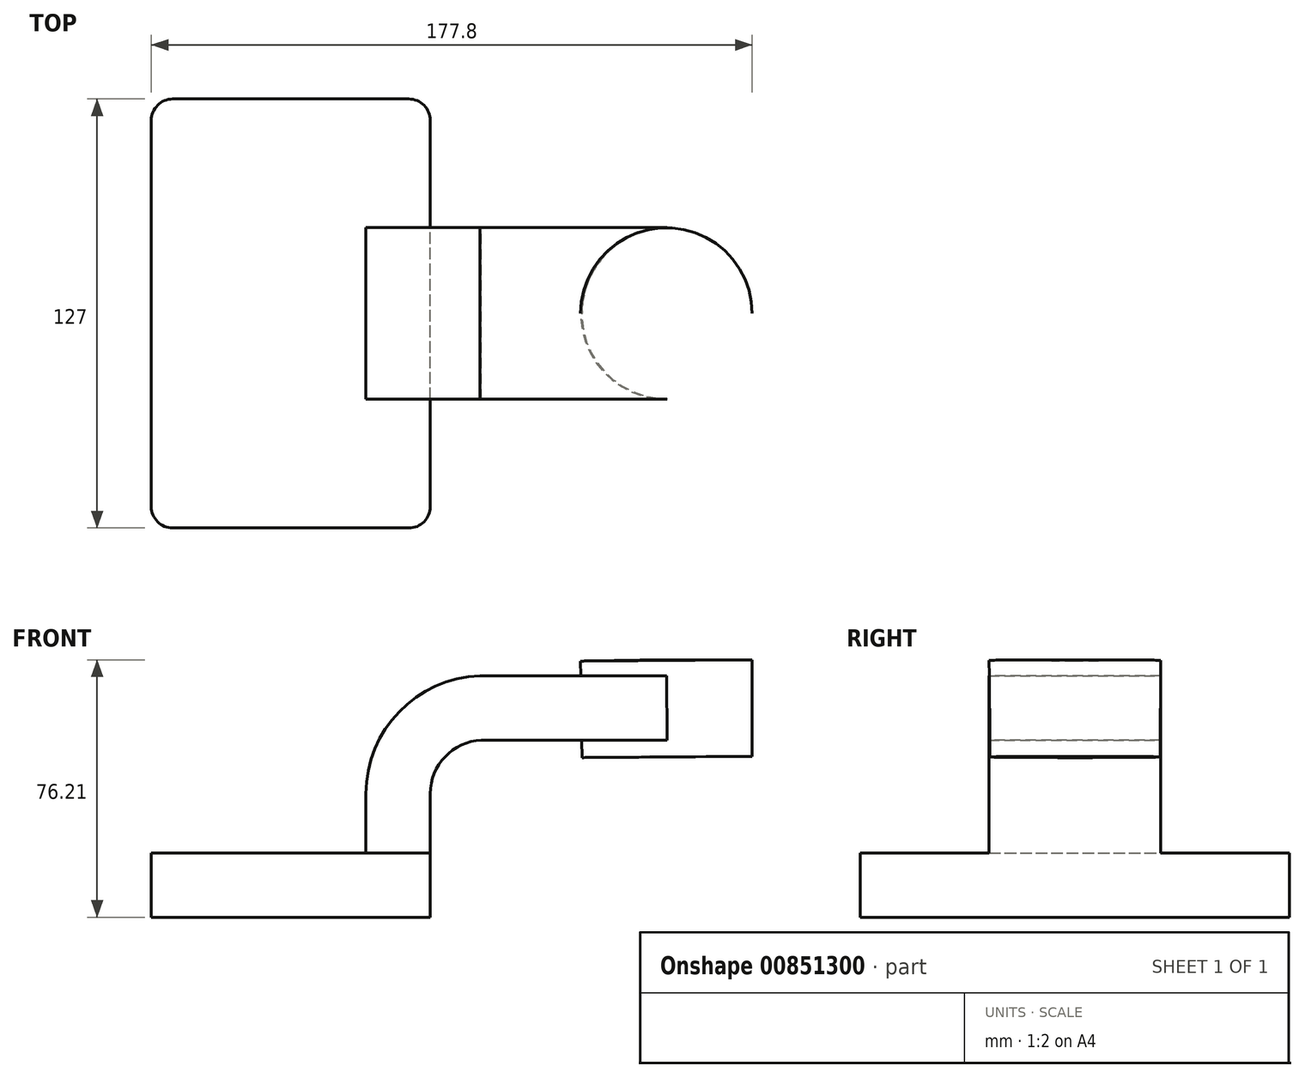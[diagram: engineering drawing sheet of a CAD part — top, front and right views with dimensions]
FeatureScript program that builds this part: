
annotation { "Feature Type Name" : "Feature", "Feature Type Description" : "" }
export const myFeature = defineFeature(function(context is Context, id is Id, definition is map)
    precondition{}
    {
        {
            var Q0;
            Q0=qCreatedBy(makeId("Front.planeOp"),FACE);
            var sketch = newSketch(context, id + "F0", { "sketchPlane" : qUnion([Q0])});
            skLineSegment(sketch, "E0.bottom", {"start": v(-41.28, -9.53) * mm, "end": v(41.28, -9.53) * mm});
            skLineSegment(sketch, "E0.top", {"start": v(-41.28, 9.53) * mm, "end": v(41.28, 9.53) * mm});
            skLineSegment(sketch, "E0.left", {"start": v(-41.28, -9.53) * mm, "end": v(-41.28, 9.53) * mm});
            skLineSegment(sketch, "E0.right", {"start": v(41.28, -9.53) * mm, "end": v(41.28, 9.52) * mm});
            skPoint(sketch, "E0.middle", {"position": v(0, 0) * mm});
            skLineSegment(sketch, "E1.bottom", {"start": v(85.72, 66.67) * mm, "end": v(136.53, 66.67) * mm});
            skLineSegment(sketch, "E1.top", {"start": v(85.72, 38.1) * mm, "end": v(136.53, 38.1) * mm});
            skLineSegment(sketch, "E1.left", {"start": v(85.72, 66.68) * mm, "end": v(85.72, 38.1) * mm});
            skLineSegment(sketch, "E1.right", {"start": v(136.53, 66.68) * mm, "end": v(136.53, 38.1) * mm});
            skPoint(sketch, "E1.middle", {"position": v(111.12, 52.39) * mm});
            skLineSegment(sketch, "E2", {"start": v(41.28, 9.52) * mm, "end": v(41.28, 27.02) * mm});
            skArc(sketch, "E3", {"start": v(41.27, 27.02) * mm, "mid": v(45.66, 37.97) * mm, "end": v(56.4, 42.88) * mm});
            skLineSegment(sketch, "E4", {"start": v(56.4, 42.88) * mm, "end": v(111.34, 42.88) * mm});
            skLineSegment(sketch, "E5.0", {"start": v(56.03, 61.93) * mm, "end": v(111.34, 61.93) * mm});
            skArc(sketch, "E5.1", {"start": v(22.22, 27.02) * mm, "mid": v(32.06, 51.31) * mm, "end": v(56.03, 61.93) * mm});
            skLineSegment(sketch, "E5.2", {"start": v(22.22, 9.52) * mm, "end": v(22.22, 27.02) * mm});
            skLineSegment(sketch, "E6", {"start": v(111.12, 66.67) * mm, "end": v(111.34, 38.1) * mm});
            skFitSpline(sketch, "E7", {"points": [v(-41.28, 9.52) * mm, v(56.03, 61.93) * mm], "startDerivative": vector(-0.08, 70.29) * mm, "endDerivative": vector(116.7, -2.88) * mm});
            skSolve(sketch);
        }
        {
            var Q0;
            Q0=makeQuery(id+"F0.imprint","IMPRINT",FACE,{"disambiguationData":[TD([[makeQuery(id+"F0.imprint","IMPRINT",EDGE,{"derivedFrom":sQuery(id+"F0.wireOp",EDGE,"E0.bottom")}),1.0]])]});
            extrude(context, id + "F1", {"entities" : qUnion([Q0]), "endBound" : BoundingType.SYMMETRIC, "depth" : 127 * mm, "offsetDistance" : 25.4 * mm});
        }
        {
            var Q0;
            {var subQ1=sQuery(id+"F0.wireOp",EDGE,"E2");Q0=makeQuery(id+"F0.imprint","IMPRINT",FACE,{"disambiguationData":[TD([[makeQuery(id+"F0.imprint","IMPRINT",EDGE,{"derivedFrom":subQ1}),1.0]])]});}
            var Q1;
            {var subQ0=sQuery(id+"F0.wireOp",EDGE,"E5.0");var subQ1=sQuery(id+"F0.wireOp",EDGE,"E1.left");var subQ2=makeQuery(id+"F0.imprint","INTERSECT",VERTEX,{"derivedFrom":[subQ1,subQ0]});Q1=makeQuery(id+"F0.imprint","IMPRINT",FACE,{"disambiguationData":[TD([[makeQuery(id+"F0.imprint","IMPRINT",EDGE,{"disambiguationData":[TD([[subQ2,-1.0]])],"derivedFrom":subQ1}),1.0]])]});}
            extrude(context, id + "F2", {"entities" : qUnion([Q0, Q1]), "operationType" : NewBodyOperationType.ADD, "endBound" : BoundingType.SYMMETRIC, "depth" : 50.8 * mm, "offsetDistance" : 25.4 * mm});
        }
        {
            var Q0;
            Q0=makeQuery(id+"F0.imprint","IMPRINT",FACE,{"disambiguationData":[TD([[makeQuery(id+"F0.imprint","IMPRINT",EDGE,{"derivedFrom":sQuery(id+"F0.wireOp",EDGE,"E5.1")}),1.0]])]});
            extrude(context, id + "F3", {"entities" : qUnion([Q0]), "operationType" : NewBodyOperationType.ADD, "endBound" : BoundingType.SYMMETRIC, "depth" : 15.88 * mm, "offsetDistance" : 25.4 * mm});
        }
        {
            var Q0;
            {var subQ0=sQuery(id+"F0.wireOp",EDGE,"E1.right");Q0=makeQuery(id+"F0.imprint","IMPRINT",FACE,{"disambiguationData":[TD([[makeQuery(id+"F0.imprint","IMPRINT",EDGE,{"derivedFrom":subQ0}),-1.0]])]});}
            var Q1;
            Q1=sQuery(id+"F0.wireOp",EDGE,"E6");
            revolve(context, id + "F4", {"operationType" : NewBodyOperationType.ADD, "surfaceOperationType" : NewSurfaceOperationType.NEW, "entities" : qUnion([Q0]), "axis" : qUnion([Q1]), "revolveType" : RevolveType.FULL});
        }
        {
            var Q0;
            Q0=makeQuery(id+"F1.opExtrude","CAP_EDGE",EDGE,{"disambiguationData":[OSD([sQuery(id+"F0.wireOp",EDGE,"E0.right")])],"isStart":false});
            var Q1;
            Q1=makeQuery(id+"F1.opExtrude","CAP_EDGE",EDGE,{"disambiguationData":[OSD([sQuery(id+"F0.wireOp",EDGE,"E0.right")])],"isStart":true});
            var Q2;
            Q2=makeQuery(id+"F1.opExtrude","CAP_EDGE",EDGE,{"disambiguationData":[OSD([sQuery(id+"F0.wireOp",EDGE,"E0.left")])],"isStart":true});
            var Q3;
            Q3=makeQuery(id+"F1.opExtrude","CAP_EDGE",EDGE,{"disambiguationData":[OSD([sQuery(id+"F0.wireOp",EDGE,"E0.left")])],"isStart":false});
            fillet(context, id + "F5", {"entities" : qUnion([Q0, Q1, Q2, Q3]), "radius" : 6.35 * mm, "tangentPropagation" : true, "allowEdgeOverflow" : false});
        }
    });
